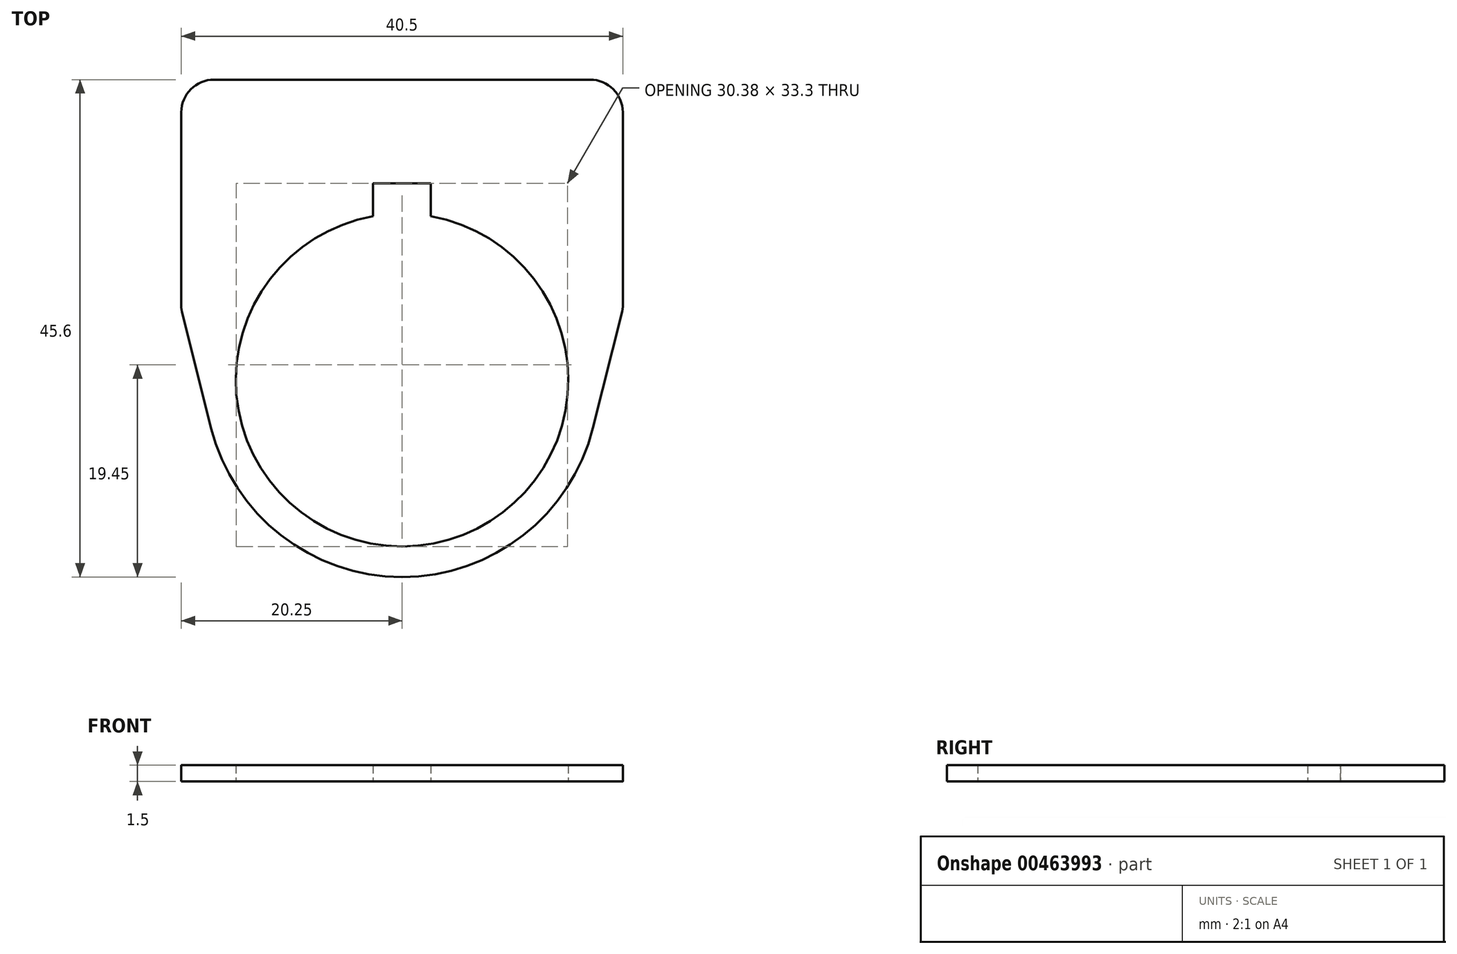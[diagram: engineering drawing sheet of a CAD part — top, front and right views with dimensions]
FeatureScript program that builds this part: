
annotation { "Feature Type Name" : "Feature", "Feature Type Description" : "" }
export const myFeature = defineFeature(function(context is Context, id is Id, definition is map)
    precondition{}
    {
        {
            var Q0;
            Q0=qCreatedBy(makeId("Top.planeOp"),FACE);
            var sketch = newSketch(context, id + "F0", { "sketchPlane" : qUnion([Q0])});
            skCircle(sketch, "E0", {"center": v(0, 0) * mm, "radius": 15.25 * mm});
            skCircle(sketch, "E1", {"center": v(0, 0) * mm, "radius": 18.05 * mm});
            skLineSegment(sketch, "E2", {"start": v(17.25, 27.55) * mm, "end": v(-17.25, 27.55) * mm});
            skLineSegment(sketch, "E3", {"start": v(20.25, 24.55) * mm, "end": v(20.25, 6.55) * mm});
            skLineSegment(sketch, "E4", {"start": v(-20.25, 24.55) * mm, "end": v(-20.25, 6.55) * mm});
            skLineSegment(sketch, "E5", {"start": v(-20.25, 6.55) * mm, "end": v(-17.5, -4.39) * mm});
            skLineSegment(sketch, "E6", {"start": v(20.25, 6.55) * mm, "end": v(17.5, -4.39) * mm});
            skLineSegment(sketch, "E7", {"start": v(2.12, -14.45) * mm, "end": v(-2.12, -14.45) * mm});
            skLineSegment(sketch, "E8", {"start": v(-2.12, -14.45) * mm, "end": v(-2.12, -15.1) * mm});
            skLineSegment(sketch, "E9", {"start": v(2.12, -14.45) * mm, "end": v(2.12, -15.1) * mm});
            skLineSegment(sketch, "E10", {"start": v(0, 18.05) * mm, "end": v(-2.65, 18.05) * mm});
            skLineSegment(sketch, "E11", {"start": v(-2.65, 18.05) * mm, "end": v(2.65, 18.05) * mm});
            skLineSegment(sketch, "E12", {"start": v(-2.65, 18.05) * mm, "end": v(-2.65, 15.02) * mm});
            skLineSegment(sketch, "E13", {"start": v(2.65, 18.05) * mm, "end": v(2.65, 15.02) * mm});
            skPoint(sketch, "E14.visualSharp", {"position": v(-20.25, 27.55) * mm});
            skArc(sketch, "E14.filletArc", {"start": v(-17.25, 27.55) * mm, "mid": v(-19.37, 26.67) * mm, "end": v(-20.25, 24.55) * mm});
            skPoint(sketch, "E15.visualSharp", {"position": v(20.25, 27.55) * mm});
            skArc(sketch, "E15.filletArc", {"start": v(20.25, 24.55) * mm, "mid": v(19.37, 26.67) * mm, "end": v(17.25, 27.55) * mm});
            skSolve(sketch);
        }
        {
            var Q0;
            Q0=makeQuery(id+"F0.imprint","IMPRINT",FACE,{"disambiguationData":[TD([[makeQuery(id+"F0.imprint","IMPRINT",EDGE,{"derivedFrom":sQuery(id+"F0.wireOp",EDGE,"E2")}),1.0]])]});
            var Q1;
            {var subQ0=sQuery(id+"F0.wireOp",EDGE,"E0");var subQ8=makeQuery(id+"F0.imprint","INTERSECT",VERTEX,{"derivedFrom":[subQ0,sQuery(id+"F0.wireOp",EDGE,"E8")]});Q1=makeQuery(id+"F0.imprint","IMPRINT",FACE,{"disambiguationData":[TD([[makeQuery(id+"F0.imprint","IMPRINT",EDGE,{"disambiguationData":[TD([[subQ8,1.0]])],"derivedFrom":subQ0}),-1.0]])]});}
            extrude(context, id + "F1", {"entities" : qUnion([Q0, Q1]), "depth" : 1.5 * mm});
        }
        {
            var Q0;
            Q0=makeQuery(id+"F1.opExtrude","SWEPT_EDGE",EDGE,{"disambiguationData":[OSD([sQuery(id+"F0.wireOp",EDGE,"E4"),sQuery(id+"F0.wireOp",EDGE,"E5")])]});
            var Q1;
            Q1=makeQuery(id+"F1.opExtrude","SWEPT_EDGE",EDGE,{"disambiguationData":[OSD([sQuery(id+"F0.wireOp",EDGE,"E3"),sQuery(id+"F0.wireOp",EDGE,"E6")])]});
            fillet(context, id + "F2", {"entities" : qUnion([Q0, Q1]), "radius" : 2 * mm, "tangentPropagation" : true, "allowEdgeOverflow" : false});
        }
    });
